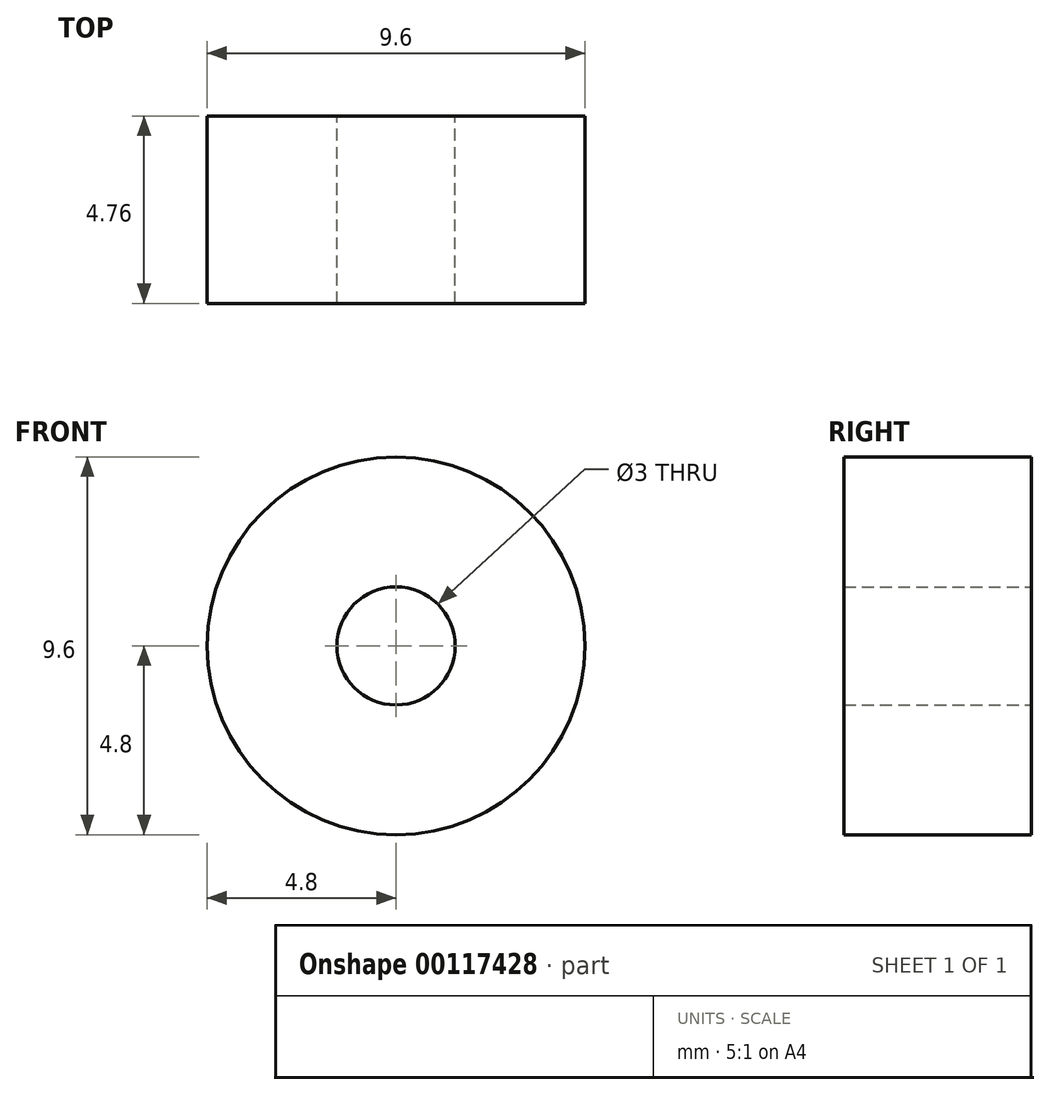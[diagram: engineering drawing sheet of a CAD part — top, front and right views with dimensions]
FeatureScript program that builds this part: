
annotation { "Feature Type Name" : "Feature", "Feature Type Description" : "" }
export const myFeature = defineFeature(function(context is Context, id is Id, definition is map)
    precondition{}
    {
        {
            var Q0;
            Q0=qCreatedBy(makeId("Front.planeOp"),FACE);
            var sketch = newSketch(context, id + "F0", { "sketchPlane" : qUnion([Q0])});
            skCircle(sketch, "E0", {"center": v(0, 0) * mm, "radius": 4.8 * mm});
            skCircle(sketch, "E1", {"center": v(0, 0) * mm, "radius": 1.5 * mm});
            skSolve(sketch);
        }
        {
            var Q0;
            Q0=makeQuery(id+"F0.imprint","IMPRINT",FACE,{"disambiguationData":[TD([[makeQuery(id+"F0.imprint","IMPRINT",EDGE,{"derivedFrom":sQuery(id+"F0.wireOp",EDGE,"E0")}),1.0]])]});
            var Q1;
            Q1=sQuery(id+"F0.wireOp",EDGE,"E1");
            var Q2;
            Q2=sQuery(id+"F0.wireOp",EDGE,"E0");
            extrude(context, id + "F1", {"entities" : qUnion([Q0]), "surfaceEntities" : qUnion([Q1, Q2]), "depth" : 4.76 * mm});
        }
    });
